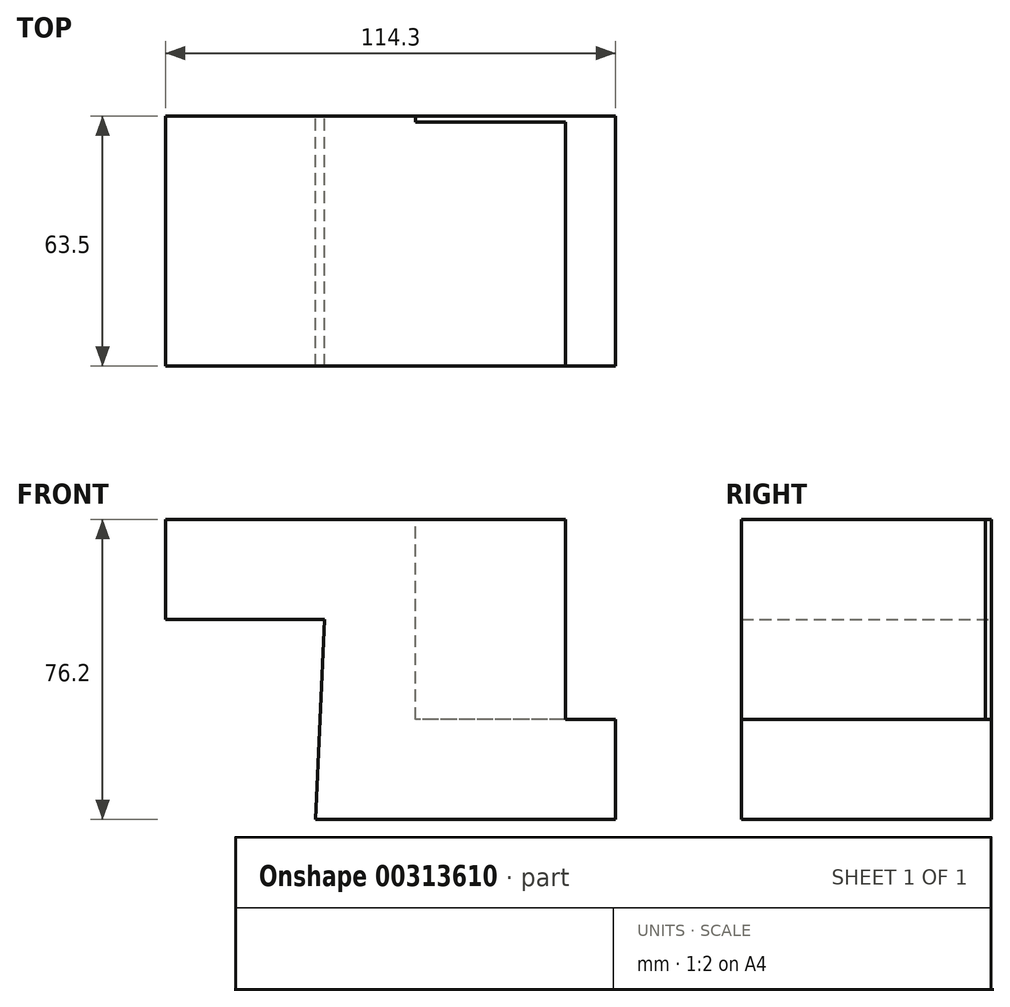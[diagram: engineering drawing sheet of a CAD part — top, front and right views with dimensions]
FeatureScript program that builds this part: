
annotation { "Feature Type Name" : "Feature", "Feature Type Description" : "" }
export const myFeature = defineFeature(function(context is Context, id is Id, definition is map)
    precondition{}
    {
        {
            var Q0;
            Q0=qCreatedBy(makeId("Front.planeOp"),FACE);
            var sketch = newSketch(context, id + "F0", { "sketchPlane" : qUnion([Q0])});
            skLineSegment(sketch, "E0", {"start": v(-28.43, -50.8) * mm, "end": v(47.77, -50.8) * mm});
            skLineSegment(sketch, "E1", {"start": v(47.77, -50.8) * mm, "end": v(47.77, -25.4) * mm});
            skLineSegment(sketch, "E2", {"start": v(47.77, -25.4) * mm, "end": v(-3.03, -25.4) * mm});
            skLineSegment(sketch, "E3", {"start": v(-3.03, -25.4) * mm, "end": v(-3.03, 25.4) * mm});
            skLineSegment(sketch, "E4", {"start": v(-3.03, 25.4) * mm, "end": v(-66.53, 25.4) * mm});
            skLineSegment(sketch, "E5", {"start": v(-66.53, 25.4) * mm, "end": v(-66.53, 0) * mm});
            skLineSegment(sketch, "E6", {"start": v(-64.26, 0) * mm, "end": v(-26.16, 0) * mm});
            skLineSegment(sketch, "E7", {"start": v(-26.16, 0) * mm, "end": v(-28.43, -50.8) * mm});
            skLineSegment(sketch, "E8", {"start": v(-66.53, 0) * mm, "end": v(-64.26, 0) * mm});
            skSolve(sketch);
        }
        {
            var Q0;
            Q0 = qSketchRegion(id + "F0", true);
            extrude(context, id + "F1", {"entities" : qUnion([Q0]), "depth" : 63.5 * mm});
        }
        {
            var Q0;
            Q0=makeQuery(id+"F1.opExtrude","CAP_FACE",FACE,{"disambiguationData":[OSD([sQuery(id+"F0.wireOp",EDGE,"E0"),sQuery(id+"F0.wireOp",EDGE,"E1"),sQuery(id+"F0.wireOp",EDGE,"E2"),sQuery(id+"F0.wireOp",EDGE,"E3"),sQuery(id+"F0.wireOp",EDGE,"E4"),sQuery(id+"F0.wireOp",EDGE,"E5"),sQuery(id+"F0.wireOp",EDGE,"E6"),sQuery(id+"F0.wireOp",EDGE,"E7"),sQuery(id+"F0.wireOp",EDGE,"E8")])],"isStart":false});
            var sketch = newSketch(context, id + "F2", { "sketchPlane" : qUnion([Q0])});
            skLineSegment(sketch, "E9", {"start": v(-3.03, 25.4) * mm, "end": v(35.07, 25.4) * mm});
            skLineSegment(sketch, "E10", {"start": v(35.07, 25.4) * mm, "end": v(35.07, -25.4) * mm});
            skSolve(sketch);
        }
        {
            var Q0;
            Q0=makeQuery(id+"F2.imprint","IMPRINT",FACE,{"disambiguationData":[TD([[makeQuery(id+"F2.imprint","IMPRINT",EDGE,{"derivedFrom":sQuery(id+"F2.wireOp",EDGE,"E9")}),-1.0]])]});
            extrude(context, id + "F3", {"entities" : qUnion([Q0]), "operationType" : NewBodyOperationType.ADD, "oppositeDirection" : true, "depth" : 61.98 * mm});
        }
    });
